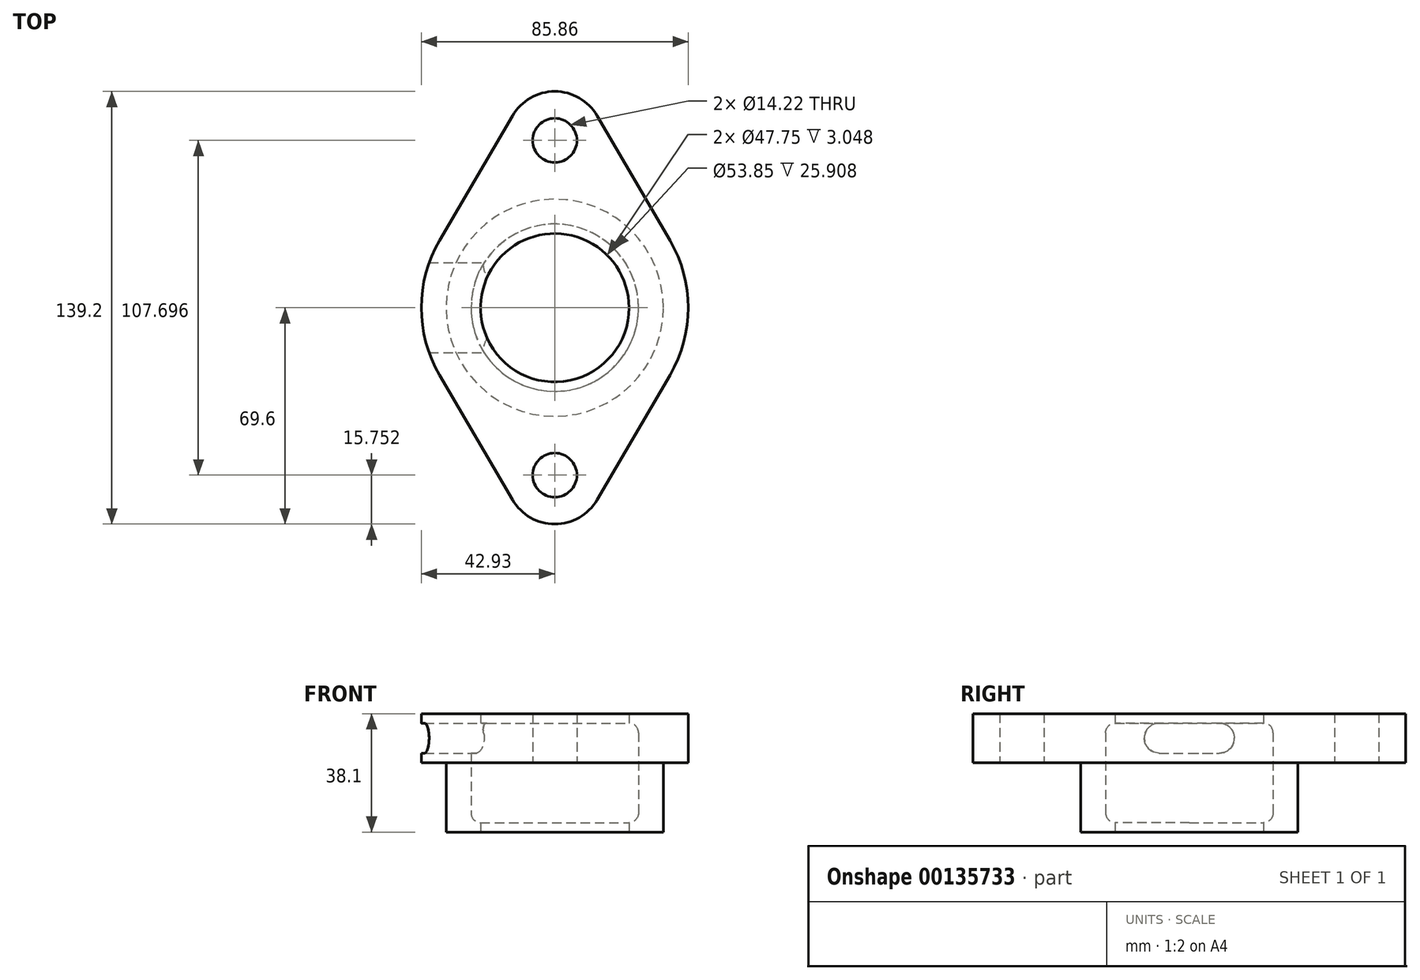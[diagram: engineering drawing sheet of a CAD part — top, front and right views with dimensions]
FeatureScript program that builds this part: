
annotation { "Feature Type Name" : "Feature", "Feature Type Description" : "" }
export const myFeature = defineFeature(function(context is Context, id is Id, definition is map)
    precondition{}
    {
        {
            var Q0;
            Q0=qCreatedBy(makeId("Top.planeOp"),FACE);
            var sketch = newSketch(context, id + "F0", { "sketchPlane" : qUnion([Q0])});
            skCircle(sketch, "E0", {"center": v(0, 53.85) * mm, "radius": 7.11 * mm});
            skCircle(sketch, "E1", {"center": v(0, -53.85) * mm, "radius": 7.11 * mm});
            skArc(sketch, "E2", {"start": v(13.6, 61.8) * mm, "mid": v(0, 69.6) * mm, "end": v(-13.6, 61.8) * mm});
            skArc(sketch, "E3", {"start": v(-13.6, -61.8) * mm, "mid": v(0, -69.6) * mm, "end": v(13.6, -61.8) * mm});
            skArc(sketch, "E4", {"start": v(-37.06, 21.67) * mm, "mid": v(-42.93, 0) * mm, "end": v(-37.06, -21.67) * mm});
            skLineSegment(sketch, "E5", {"start": v(13.6, 61.8) * mm, "end": v(37.06, 21.67) * mm});
            skLineSegment(sketch, "E6", {"start": v(13.6, -61.8) * mm, "end": v(37.06, -21.67) * mm});
            skLineSegment(sketch, "E7", {"start": v(-13.6, 61.8) * mm, "end": v(-37.06, 21.67) * mm});
            skLineSegment(sketch, "E8", {"start": v(-13.6, -61.8) * mm, "end": v(-37.06, -21.67) * mm});
            skArc(sketch, "E9.trimOffspring", {"start": v(37.06, -21.67) * mm, "mid": v(42.93, 0) * mm, "end": v(37.06, 21.67) * mm});
            skSolve(sketch);
        }
        {
            var Q0;
            Q0 = qSketchRegion(id + "F0", true);
            extrude(context, id + "F1", {"entities" : qUnion([Q0]), "depth" : 38.1 * mm});
        }
        {
            var Q0;
            Q0=qCreatedBy(makeId("Right.planeOp"),FACE);
            var sketch = newSketch(context, id + "F2", { "sketchPlane" : qUnion([Q0])});
            skArc(sketch, "E10", {"start": v(9.65, 25.4) * mm, "mid": v(14.48, 30.23) * mm, "end": v(9.65, 35.05) * mm});
            skLineSegment(sketch, "E11", {"start": v(-9.65, 35.05) * mm, "end": v(9.65, 35.05) * mm});
            skArc(sketch, "E12", {"start": v(-9.65, 35.05) * mm, "mid": v(-14.48, 30.23) * mm, "end": v(-9.65, 25.4) * mm});
            skLineSegment(sketch, "E13", {"start": v(-9.65, 25.4) * mm, "end": v(9.65, 25.4) * mm});
            skSolve(sketch);
        }
        {
            var Q0;
            Q0 = qSketchRegion(id + "F2", true);
            var Q1;
            Q1=makeQuery(id+"F1.opExtrude","SWEPT_FACE",FACE,{"disambiguationData":[OSD([sQuery(id+"F0.wireOp",EDGE,"E4")])]});
            extrude(context, id + "F3", {"entities" : qUnion([Q0]), "operationType" : NewBodyOperationType.REMOVE, "endBound" : BoundingType.UP_TO_SURFACE, "oppositeDirection" : true, "endBoundEntityFace" : qUnion([Q1]), "depth" : 25.4 * mm});
        }
        {
            var Q0;
            Q0=qCreatedBy(makeId("Front.planeOp"),FACE);
            var sketch = newSketch(context, id + "F4", { "sketchPlane" : qUnion([Q0])});
            skLineSegment(sketch, "E14.bottom", {"start": v(0, 3.05) * mm, "end": v(23.88, 3.05) * mm});
            skLineSegment(sketch, "E14.top", {"start": v(0, 35.05) * mm, "end": v(23.88, 35.05) * mm});
            skLineSegment(sketch, "E14.left", {"start": v(0, 3.05) * mm, "end": v(0, 35.05) * mm});
            skLineSegment(sketch, "E14.right", {"start": v(26.92, 6.1) * mm, "end": v(26.92, 32) * mm});
            skPoint(sketch, "E15.visualSharp", {"position": v(26.92, 35.05) * mm});
            skArc(sketch, "E15.filletArc", {"start": v(26.92, 32) * mm, "mid": v(26.03, 34.16) * mm, "end": v(23.88, 35.05) * mm});
            skPoint(sketch, "E16.visualSharp", {"position": v(26.92, 3.05) * mm});
            skArc(sketch, "E16.filletArc", {"start": v(23.88, 3.05) * mm, "mid": v(26.03, 3.94) * mm, "end": v(26.92, 6.1) * mm});
            skSolve(sketch);
        }
        {
            var Q0;
            Q0 = qSketchRegion(id + "F4", true);
            var Q1;
            Q1=sQuery(id+"F4.wireOp",EDGE,"E14.left");
            revolve(context, id + "F5", {"operationType" : NewBodyOperationType.REMOVE, "entities" : qUnion([Q0]), "axis" : qUnion([Q1]), "revolveType" : RevolveType.FULL});
        }
        {
            var Q0;
            Q0=makeQuery(id+"F1.opExtrude","CAP_FACE",FACE,{"disambiguationData":[OSD([sQuery(id+"F0.wireOp",EDGE,"E0"),sQuery(id+"F0.wireOp",EDGE,"E1"),sQuery(id+"F0.wireOp",EDGE,"E2"),sQuery(id+"F0.wireOp",EDGE,"E3"),sQuery(id+"F0.wireOp",EDGE,"E4"),sQuery(id+"F0.wireOp",EDGE,"E5"),sQuery(id+"F0.wireOp",EDGE,"E6"),sQuery(id+"F0.wireOp",EDGE,"E7"),sQuery(id+"F0.wireOp",EDGE,"E8"),sQuery(id+"F0.wireOp",EDGE,"E9.trimOffspring")])],"isStart":true});
            var sketch = newSketch(context, id + "F6", { "sketchPlane" : qUnion([Q0])});
            skCircle(sketch, "E17", {"center": v(0, 0) * mm, "radius": 23.88 * mm});
            skSolve(sketch);
        }
        {
            var Q0;
            Q0=makeQuery(id+"F6.imprint","IMPRINT",FACE,{"disambiguationData":[TD([[makeQuery(id+"F6.imprint","IMPRINT",EDGE,{"derivedFrom":sQuery(id+"F6.wireOp",EDGE,"E17")}),1.0]])]});
            extrude(context, id + "F7", {"entities" : qUnion([Q0]), "operationType" : NewBodyOperationType.REMOVE, "endBound" : BoundingType.THROUGH_ALL, "oppositeDirection" : true, "depth" : 25.4 * mm});
        }
        {
            var Q0;
            Q0=makeQuery(id+"F1.opExtrude","CAP_FACE",FACE,{"disambiguationData":[OSD([sQuery(id+"F0.wireOp",EDGE,"E0"),sQuery(id+"F0.wireOp",EDGE,"E1"),sQuery(id+"F0.wireOp",EDGE,"E2"),sQuery(id+"F0.wireOp",EDGE,"E3"),sQuery(id+"F0.wireOp",EDGE,"E4"),sQuery(id+"F0.wireOp",EDGE,"E5"),sQuery(id+"F0.wireOp",EDGE,"E6"),sQuery(id+"F0.wireOp",EDGE,"E7"),sQuery(id+"F0.wireOp",EDGE,"E8"),sQuery(id+"F0.wireOp",EDGE,"E9.trimOffspring")])],"isStart":true});
            var sketch = newSketch(context, id + "F8", { "sketchPlane" : qUnion([Q0])});
            skCircle(sketch, "E18", {"center": v(0, 0) * mm, "radius": 34.93 * mm});
            skLineSegment(sketch, "E19.bottom", {"start": v(-42.93, 69.6) * mm, "end": v(42.93, 69.6) * mm});
            skLineSegment(sketch, "E19.top", {"start": v(-42.93, -69.85) * mm, "end": v(42.93, -69.85) * mm});
            skLineSegment(sketch, "E19.left", {"start": v(-42.93, 69.6) * mm, "end": v(-42.93, -69.85) * mm});
            skLineSegment(sketch, "E19.right", {"start": v(42.93, 69.6) * mm, "end": v(42.93, -69.85) * mm});
            skSolve(sketch);
        }
        {
            var Q0;
            Q0 = qSketchRegion(id + "F8", true);
            extrude(context, id + "F9", {"entities" : qUnion([Q0]), "operationType" : NewBodyOperationType.REMOVE, "oppositeDirection" : true, "depth" : 22.35 * mm});
        }
    });
